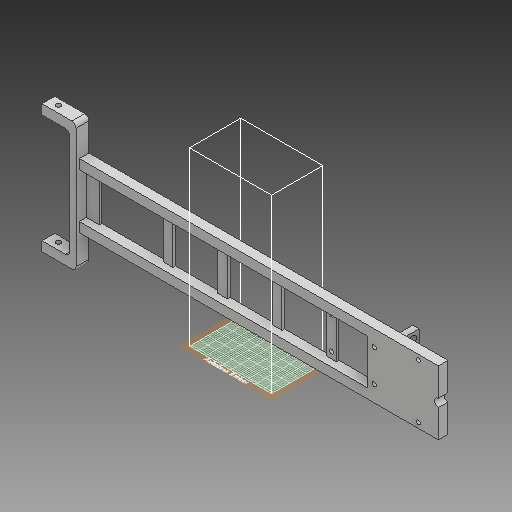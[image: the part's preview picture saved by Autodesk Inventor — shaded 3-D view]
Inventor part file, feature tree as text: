
AUTODESK INVENTOR PART (.ipt)
format: ipt  version: 2018 (Build 220112000, 112)  size: 616,448 bytes
history: native  units: mm
features: sketch x33, extrude x25, hole x6, fillet x6
ambient origin geometry x8: Origin, YZ Plane, XZ Plane, XY Plane, X Axis, Y Axis, Z Axis, Center Point
bodies: Solid1 (feature_tree)
feature tree (70):
  extrude  "Extrusion1"  Depth=50.0mm
  hole  "Hole1"  [1 undecoded]
  hole  "Hole2"  [1 undecoded]
  extrude  "Extrusion2"  Depth=25.0mm
  extrude  "Extrusion3"  Depth=25.0mm
  extrude  "Extrusion4"  Depth=5.0mm
  sketch  "Sketch7"  dims[d25=10.0mm d26=5.0mm]
  extrude  "Extrusion5"  Depth=5.0mm
  extrude  "Extrusion6"  Depth=35.0mm
  extrude  "Extrusion7"  Depth=35.0mm
  extrude  "Extrusion8"  Depth=35.0mm
  extrude  "Extrusion9"  Depth=2.0mm TaperAngle=0.0deg
  extrude  "Extrusion10"  Depth=7.5mm TaperAngle=0.0deg
  extrude  "Extrusion11"  Depth=10.0mm
  extrude  "Extrusion12"  Depth=7.5mm
  fillet  "Fillet1"  Radius=7.5mm
  fillet  "Fillet2"  Radius=25.0mm
  fillet  "Fillet3"  Radius=3.0mm
  fillet  "Fillet4"  Radius=3.2mm
  fillet  "Fillet5"  Radius=2.1mm
  fillet  "Fillet6"  Radius=5.5mm
  extrude  "Extrusion13"  Depth=92.5mm TaperAngle=0.0deg
  sketch  "Sketch17"  dims[d58=4.25mm d59=241.0mm d60=0.0mm]
  hole  "Hole3"  [1 undecoded]
  hole  "Hole4"  [1 undecoded]
  extrude  "Extrusion14"  Depth=5.0mm
  extrude  "Extrusion15"  Depth=91.25mm TaperAngle=0.0deg
  extrude  "Extrusion16"  Depth=30.0mm
  extrude  "Extrusion17"  Depth=2.5mm
  extrude  "Extrusion18"  Depth=14.55mm TaperAngle=0.0deg
  extrude  "Extrusion19"  Depth=0.1mm
  extrude  "Extrusion20"  Depth=3.25mm
  extrude  "Extrusion21"  Depth=3.25mm
  hole  "Hole5"  [1 undecoded]
  extrude  "Extrusion22"  Depth=2.0mm
  extrude  "Extrusion23"  Depth=15.0mm
  extrude  "Extrusion24"  Depth=10.0mm TaperAngle=0.0deg
  extrude  "Extrusion25"  Depth=2.0mm
  hole  "Hole6"  [1 undecoded]
  sketch  "Sketch1"  dims[d0=50.0mm d1=50.0mm]
  sketch  "Sketch2"  dims[d2=240.0mm d3=7.5mm]
  sketch  "Sketch3"  dims[d4=7.5mm d5=7.5mm d6=0.0mm]
  sketch  "Sketch4"  dims[d7=6.35mm d8=6.0mm d9=4.0mm d10=2.0mm d11=90.0deg d12=8.0mm d13=20.594885mm d14=25.0mm]
  sketch  "Sketch5"  dims[d15=3.3mm d16=6.0mm d17=4.0mm d18=2.0mm d19=90.0deg d20=8.0mm d21=20.594885mm d22=25.0mm]
  sketch  "Sketch6"  dims[d23=180.0deg d24=5.0mm]
  sketch  "Sketch8"  dims[d27=17.5mm d28=0.0mm d30=35.0mm]
  sketch  "Sketch9"  dims[d31=35.0mm d32=35.0mm]
  sketch  "Sketch10"  dims[d33=35.0mm d34=35.0mm]
  sketch  "Sketch11"  dims[d35=35.0mm d36=2.0mm d37=0.0mm]
  sketch  "Sketch12"  dims[d38=10.0mm d39=7.5mm d40=0.0mm]
  sketch  "Sketch13"  dims[d41=100.0mm d42=10.0mm]
  sketch  "Sketch14"  dims[d43=7.5mm d44=0.0mm d45=7.5mm d46=7.5mm d47=25.0mm d48=0.0mm d49=3.0mm d50=3.2mm d51=2.1mm d52=5.5mm]
  sketch  "Sketch15"  dims[d53=3.3mm d54=92.5mm d55=0.0mm]
  sketch  "Sketch16"  dims[d56=5.5mm d57=3.3mm]
  sketch  "Sketch18"  dims[d61=4.44mm d62=5.0mm]
  sketch  "Sketch19"  dims[d63=2.5mm d64=91.25mm d65=0.0mm]
  sketch  "Sketch20"  dims[d66=30.0mm d67=6.35mm]
  sketch  "Sketch21"  dims[d68=3.8mm d69=0.0mm d70=2.5mm]
  sketch  "Sketch22"  dims[d71=14.55mm d72=0.0mm d73=14.55mm d74=0.0mm]
  sketch  "Sketch23"  dims[d75=0.1mm d76=0.1mm]
  sketch  "Sketch24"  dims[d77=3.25mm d78=3.25mm]
  sketch  "Sketch25"  dims[d79=3.25mm d80=3.25mm]
  sketch  "Sketch26"  dims[d81=35.0mm d82=10.0mm]
  sketch  "Sketch27"  dims[d83=2.0mm d84=0.0mm d85=3.6mm]
  sketch  "Sketch28"  dims[d86=3.6mm]
  sketch  "Sketch29"  dims[d87=3.3mm d88=6.0mm d89=4.0mm d90=2.0mm d91=90.0deg d92=15.0mm d93=20.594885mm]
  sketch  "Sketch30"  dims[d94=3.3mm d95=6.0mm d96=4.0mm d97=2.0mm d98=90.0deg d99=15.0mm d100=20.594885mm d101=6.0mm]
  sketch  "Sketch31"  dims[d102=20.0mm d103=0.0mm d104=10.0mm d105=0.0mm]
  sketch  "Sketch32"  dims[d106=2.0mm d107=0.0mm d108=4.0mm]
  sketch  "Sketch33"  dims[d109=100.0mm d110=0.0mm d111=100.0mm d112=0.0mm d113=5.0mm d114=2.0mm d115=0.0mm d116=3.3mm d117=3.3mm d118=3.3mm d119=3.3mm d120=2.0mm d121=0.0mm d122=5.5mm d123=0.0mm d124=3.3mm d125=6.0mm d126=4.0mm d127=2.0mm d128=90.0deg d129=8.0mm d130=20.594885mm d131=42.0mm d132=17.0mm d133=21.0mm d135=8.5mm d136=15.825mm d137=3.5mm d138=21.0mm d139=3.3mm d140=3.3mm d141=3.3mm d142=10.0mm d143=0.0mm d144=7.5mm d145=0.0mm d146=1000.0mm d147=0.0mm d148=10.0mm d149=10.0mm d150=10.0mm d151=0.0mm d152=6.25mm d153=6.0mm d154=4.0mm d155=2.0mm d156=90.0deg d157=8.0mm d158=0.0mm]
note: 6 required parameter values undecoded (feature->parameter linkage not recoverable at this tier; creation-order binding heuristic only, values carry confidence <= 0.55)
